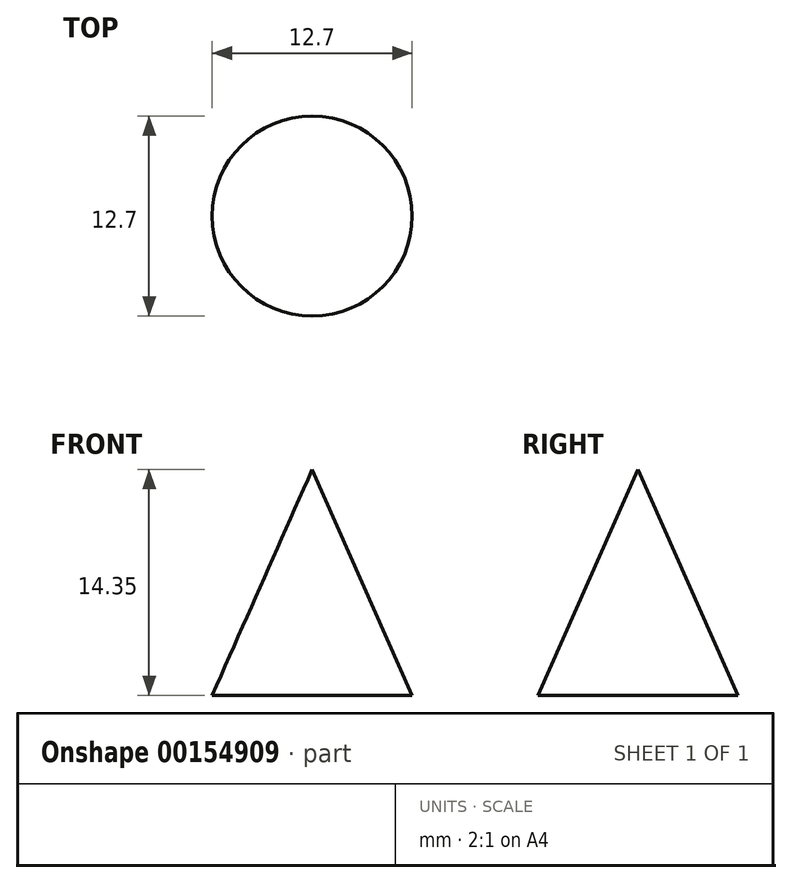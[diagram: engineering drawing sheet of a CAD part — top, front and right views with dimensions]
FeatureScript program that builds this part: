
annotation { "Feature Type Name" : "Feature", "Feature Type Description" : "" }
export const myFeature = defineFeature(function(context is Context, id is Id, definition is map)
    precondition{}
    {
        {
            var Q0;
            Q0=qCreatedBy(makeId("Right.planeOp"),FACE);
            var sketch = newSketch(context, id + "F0", { "sketchPlane" : qUnion([Q0])});
            skLineSegment(sketch, "E0", {"start": v(0, 0) * mm, "end": v(0, 14.35) * mm});
            skLineSegment(sketch, "E1", {"start": v(0, 14.35) * mm, "end": v(-6.35, 0) * mm});
            skLineSegment(sketch, "E2", {"start": v(-6.35, 0) * mm, "end": v(0, 0) * mm});
            skSolve(sketch);
        }
        {
            var Q0;
            Q0 = qSketchRegion(id + "F0", true);
            var Q1;
            Q1=sQuery(id+"F0.wireOp",EDGE,"E0");
            revolve(context, id + "F1", {"entities" : qUnion([Q0]), "axis" : qUnion([Q1]), "revolveType" : RevolveType.FULL});
        }
    });
